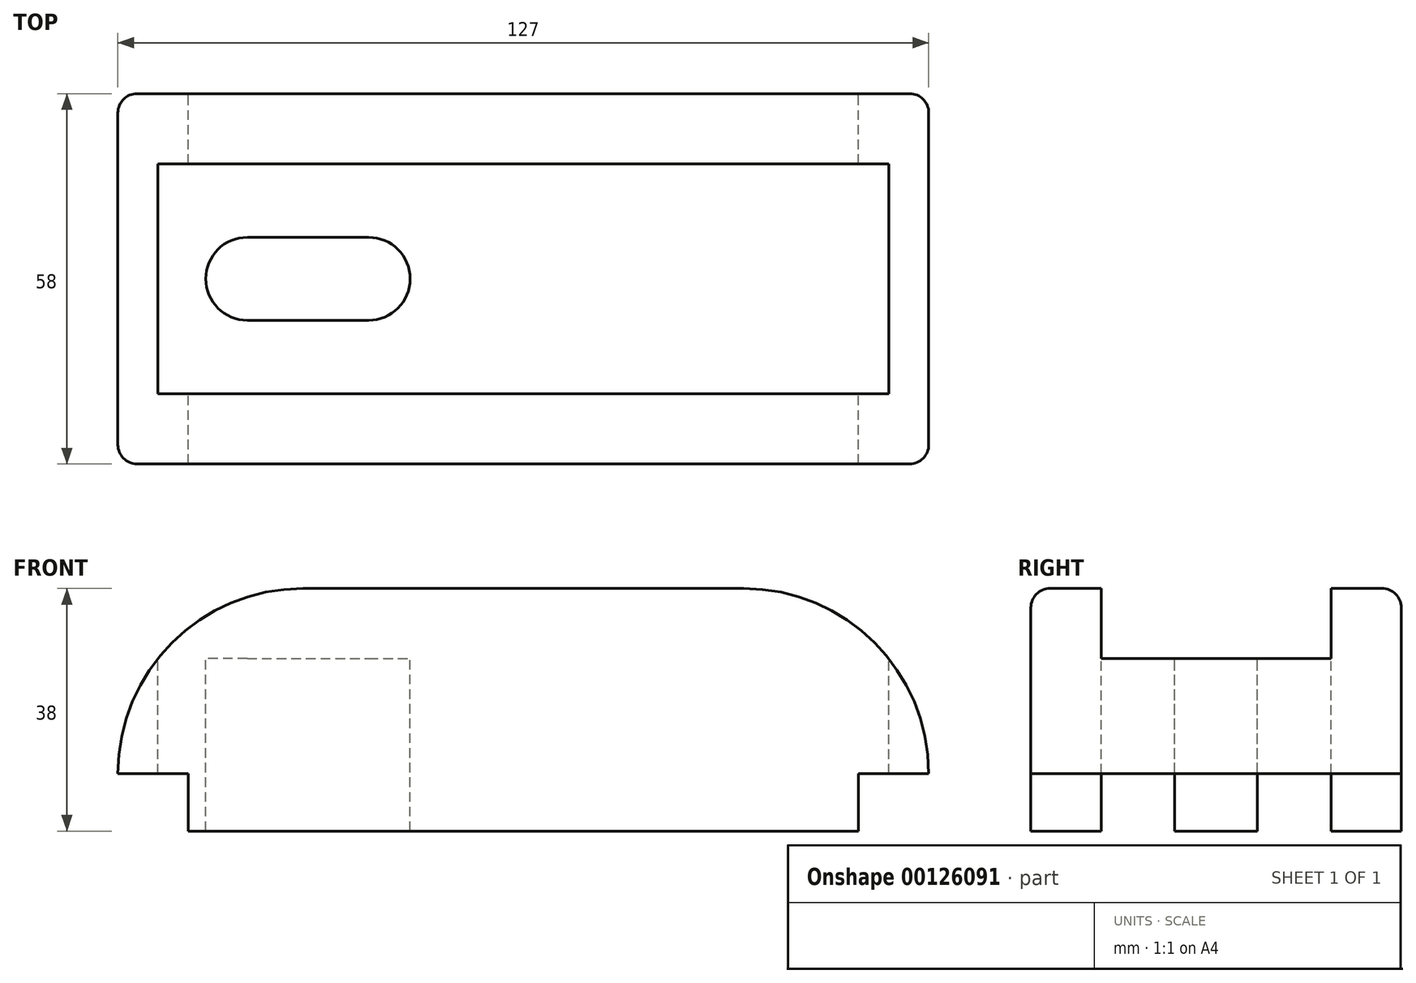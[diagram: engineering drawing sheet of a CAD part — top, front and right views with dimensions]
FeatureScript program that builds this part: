
annotation { "Feature Type Name" : "Feature", "Feature Type Description" : "" }
export const myFeature = defineFeature(function(context is Context, id is Id, definition is map)
    precondition{}
    {
        {
            var Q0;
            Q0=qCreatedBy(makeId("Front.planeOp"),FACE);
            var sketch = newSketch(context, id + "F0", { "sketchPlane" : qUnion([Q0])});
            skLineSegment(sketch, "E0", {"start": v(-52.5, 0) * mm, "end": v(52.5, 0) * mm});
            skLineSegment(sketch, "E1", {"start": v(-52.5, 0) * mm, "end": v(-52.5, 9) * mm});
            skLineSegment(sketch, "E2", {"start": v(-52.5, 9) * mm, "end": v(-63.5, 9) * mm});
            skLineSegment(sketch, "E3", {"start": v(-34.5, 38) * mm, "end": v(34.5, 38) * mm});
            skArc(sketch, "E4", {"start": v(-34.5, 38) * mm, "mid": v(-55, 29.5) * mm, "end": v(-63.5, 9) * mm});
            skArc(sketch, "E5.MirrorCS", {"start": v(34.5, 38) * mm, "mid": v(55, 29.5) * mm, "end": v(63.5, 9) * mm});
            skLineSegment(sketch, "E6.MirrorCS", {"start": v(52.5, 9) * mm, "end": v(63.5, 9) * mm});
            skLineSegment(sketch, "E7.MirrorCS", {"start": v(52.5, 0) * mm, "end": v(52.5, 9) * mm});
            skLineSegment(sketch, "E8", {"start": v(57.24, 27) * mm, "end": v(-57.24, 27) * mm});
            skSolve(sketch);
        }
        {
            var Q0;
            Q0=makeQuery(id+"F0.imprint","IMPRINT",FACE,{"disambiguationData":[TD([[makeQuery(id+"F0.imprint","IMPRINT",EDGE,{"derivedFrom":sQuery(id+"F0.wireOp",EDGE,"E0")}),1.0]])]});
            var Q1;
            {var subQ0=sQuery(id+"F0.wireOp",EDGE,"E3");Q1=makeQuery(id+"F0.imprint","IMPRINT",FACE,{"disambiguationData":[TD([[makeQuery(id+"F0.imprint","IMPRINT",EDGE,{"derivedFrom":subQ0}),-1.0]])]});}
            extrude(context, id + "F1", {"entities" : qUnion([Q0, Q1]), "endBound" : BoundingType.SYMMETRIC, "depth" : 58 * mm});
        }
        {
            var Q0;
            {var subQ0=sQuery(id+"F0.wireOp",EDGE,"E3");Q0=makeQuery(id+"F0.imprint","IMPRINT",FACE,{"disambiguationData":[TD([[makeQuery(id+"F0.imprint","IMPRINT",EDGE,{"derivedFrom":subQ0}),-1.0]])]});}
            extrude(context, id + "F2", {"entities" : qUnion([Q0]), "operationType" : NewBodyOperationType.REMOVE, "endBound" : BoundingType.SYMMETRIC, "oppositeDirection" : true, "depth" : 36 * mm});
        }
        {
            var Q0;
            Q0=makeQuery(id+"F2.boolean.opBoolean","COPY",FACE,{"derivedFrom":makeQuery(id+"F2.opExtrude","SWEPT_FACE",FACE,{"disambiguationData":[OSD([sQuery(id+"F0.wireOp",EDGE,"E8")])]})});
            var sketch = newSketch(context, id + "F3", { "sketchPlane" : qUnion([Q0])});
            skLineSegment(sketch, "E9", {"start": v(-57.24, 0) * mm, "end": v(-43.24, 0) * mm, "construction": true});
            skPoint(sketch, "E9.endSnap0", {"position": v(-57.24, 0) * mm});
            skLineSegment(sketch, "E10", {"start": v(-43.24, 0) * mm, "end": v(-24.24, 0) * mm, "construction": true});
            skArc(sketch, "E11.0.startCap", {"start": v(-43.24, -6.5) * mm, "mid": v(-49.74, 0) * mm, "end": v(-43.24, 6.5) * mm});
            skArc(sketch, "E11.0.endCap", {"start": v(-24.24, 6.5) * mm, "mid": v(-17.74, 0) * mm, "end": v(-24.24, -6.5) * mm});
            skLineSegment(sketch, "E11.0.left", {"start": v(-43.24, 6.5) * mm, "end": v(-24.24, 6.5) * mm});
            skLineSegment(sketch, "E11.0.right", {"start": v(-43.24, -6.5) * mm, "end": v(-24.24, -6.5) * mm});
            skLineSegment(sketch, "E12.MirrorCS", {"start": v(43.24, 6.5) * mm, "end": v(24.24, 6.5) * mm});
            skArc(sketch, "E13.MirrorCS", {"start": v(24.24, 6.5) * mm, "mid": v(17.74, 0) * mm, "end": v(24.24, -6.5) * mm});
            skLineSegment(sketch, "E14.MirrorCS", {"start": v(43.24, -6.5) * mm, "end": v(24.24, -6.5) * mm});
            skArc(sketch, "E15.MirrorCS", {"start": v(43.24, -6.5) * mm, "mid": v(49.74, 0) * mm, "end": v(43.24, 6.5) * mm});
            skSolve(sketch);
        }
        {
            var Q0;
            Q0=makeQuery(id+"F3.imprint","IMPRINT",FACE,{"disambiguationData":[TD([[makeQuery(id+"F3.imprint","IMPRINT",EDGE,{"derivedFrom":sQuery(id+"F3.wireOp",EDGE,"E12.MirrorCS")}),1.0]])]});
            var Q1;
            Q1=makeQuery(id+"F3.imprint","IMPRINT",FACE,{"disambiguationData":[TD([[makeQuery(id+"F3.imprint","IMPRINT",EDGE,{"derivedFrom":sQuery(id+"F3.wireOp",EDGE,"E11.0.startCap")}),-1.0]])]});
            extrude(context, id + "F4", {"entities" : qUnion([Q0, Q1]), "operationType" : NewBodyOperationType.REMOVE, "endBound" : BoundingType.THROUGH_ALL, "oppositeDirection" : true, "depth" : 25 * mm});
        }
        {
            var Q0;
            Q0=makeQuery(id+"F1.opExtrude","CAP_EDGE",EDGE,{"disambiguationData":[OSD([sQuery(id+"F0.wireOp",EDGE,"E3")])],"isStart":false});
            var Q1;
            Q1=makeQuery(id+"F1.opExtrude","CAP_EDGE",EDGE,{"disambiguationData":[OSD([sQuery(id+"F0.wireOp",EDGE,"E3")])],"isStart":true});
            fillet(context, id + "F5", {"entities" : qUnion([Q0, Q1]), "radius" : 3 * mm, "tangentPropagation" : true, "allowEdgeOverflow" : false});
        }
    });
